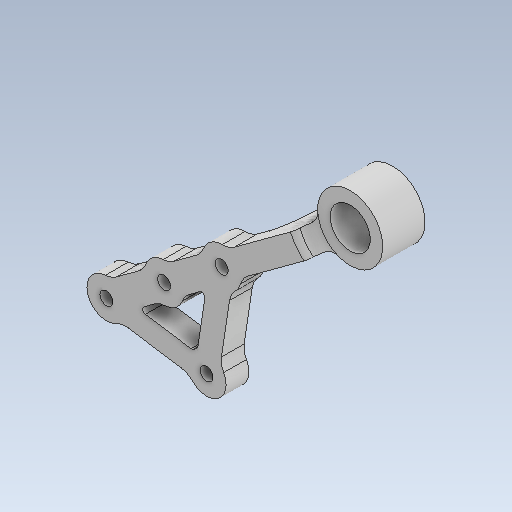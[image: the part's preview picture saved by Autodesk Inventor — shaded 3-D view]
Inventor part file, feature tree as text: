
AUTODESK INVENTOR PART (.ipt)
format: ipt  version: 2023 (Build 270158000, 158)  size: 355,840 bytes
history: native  units: mm
features: extrude x8, sketch x8, fillet x7, projected_geometry x7, other x4, reference x2, plane x1, thicken_offset x1
ambient origin geometry x8: Origin, YZ Plane, XZ Plane, XY Plane, X Axis, Y Axis, Z Axis, Center Point
bodies: Solid1 (feature_tree)
feature tree (38):
  extrude  "Extrusion1"  Depth=10.0mm
  sketch  "Sketch2"  dims[d2=2.0mm d3=11.0mm]
  plane  "Work Plane1"
  extrude  "Extrusion2"  Depth=2.0mm
  thicken_offset  "Thicken1"
  extrude  "Extrusion3"  Depth=4.0mm
  extrude  "Extrusion4"  Depth=3.5mm TaperAngle=0.0deg
  extrude  "Extrusion5"  Depth=10.0mm TaperAngle=0.0deg
  extrude  "Extrusion6"  Depth=1.5mm
  fillet  "Fillet1"  Radius=6.0mm
  fillet  "Fillet2"  Radius=6.0mm
  fillet  "Fillet3"  Radius=7.0mm
  fillet  "Fillet4"  Radius=6.15mm
  fillet  "Fillet5"  Radius=9.0mm
  extrude  "Extrusion7"  Depth=2.0mm TaperAngle=0.0deg
  extrude  "Extrusion8"  Depth=2.0mm TaperAngle=0.0deg
  fillet  "Fillet6"  Radius=4.0mm
  fillet  "Fillet7"  Radius=2.0mm
  sketch  "Sketch1"  dims[d0=10.0mm d1=11.0mm]
  reference  "Reference1"
  reference  "Reference2"
  projected_geometry  "Projected Loop1"
  sketch  "Sketch3"  dims[d4=2.0mm d5=4.0mm]
  projected_geometry  "Projected Loop2"
  sketch  "Sketch4"  dims[d6=3.5mm d7=7.0mm d8=0.0mm]
  projected_geometry  "Projected Loop3"
  sketch  "Sketch5"  dims[d9=10.0mm d10=7.0mm d11=0.0mm]
  projected_geometry  "Projected Loop4"
  sketch  "Sketch6"  dims[d12=1.5mm d13=1.5mm d14=6.0mm d15=6.0mm d16=7.0mm d17=0.0mm d18=6.15mm d19=9.0mm d20=0.0mm]
  projected_geometry  "Projected Loop5"
  sketch  "Sketch7"  dims[d21=2.0mm d22=9.0mm d23=0.0mm]
  projected_geometry  "Projected Loop6"
  sketch  "Sketch8"  dims[d24=14.0mm d25=2.0mm d26=0.0mm d30=4.0mm d31=2.0mm d32=2.0mm d33=2.0mm d34=1.0mm d35=6.0mm d36=3.5mm d37=0.0mm d38=11.0mm d39=2.0mm d40=3.5mm d42=6.0mm d43=3.5mm d44=6.0mm d45=3.5mm d46=0.0mm d47=3.0mm d48=0.5mm]
  projected_geometry  "Projected Loop7"
  parser-record x1  (decoder bookkeeping rows leaked as tree rows — omitted from the tree; the rows remain in map.json)
  other  "leg_1.iam"
  other  "leg_link_3:1"
  other  "reducer_1:1"
note: 1 file-system path scrubbed to <path> (originals preserved in map.json)
